# Revit family: Storage-Multi_Level_Workstations-Teknion-BSSCM_Cover_for_Height_Adjustable_Mechanism-R2018
name_source: partatom
category: Furniture
revit_build: Autodesk Revit 2018 (Build: 20170223_1515(x64)
units: mm (PartAtom-declared; Revit-internal decimal feet)

## family parameters
Always vertical = Yes
Cut with Voids When Loaded = No
OmniClass Number = 23.40.20.00
OmniClass Title = General Furniture and Specialties
Room Calculation Point = No
Shared = Yes
Work Plane-Based = No

## types (5) — shared parameters
Assembly Code = E2020200
Manufacturer = Teknion
Manufacturer Fax = 416.661.4586
Part Number = BSSCM
Product Documentation Link = https://www.teknion.com
Product Line = Expansion Casegoods
Product Page URL = https://www.teknion.com
Series = Expansion Casegoods
Sustainability Data = https://www.teknion.com
URL = www.teknion.com
Unit Weight URL = http://www.teknion.com
Warranty = http://www.teknion.com

## per-type parameters (varying)
| type | 1 3/16" Worksurface Thickness | Description | Full Secondary Desk Width Position | Insertion Point Offset | Model | Origin Point Offset |
| Center Position, No Width Reduction, in front of HA Mechanism | Yes | Cover for Height-Adjustable Mechanism, Center Position, No Width Reduction, In Front of Height-Adjustable Mechanism | No | 1.135 " | BSSCMCNY_____ | 1.97 " |
| End - Off-Module Position, End - 1 3/16" thick Secondary Desk, in front of HA Mechanism | Yes | Cover for Height-Adjustable Mechanism, End - Off-Module Position, End-1 3/16" thick Secondary Desk, In Front of Height-Adjustable Mechanism | No | 1.135 " | BSSCMEMY_____ | 7.315 " |
| End - Off-Module Position, End - 1 9/16" thick Secondary Desk, in front of HA Mechanism | No | Cover for Height-Adjustable Mechanism, End - Off-Module Position, End-1 9/16" thick Secondary Desk, In Front of Height-Adjustable Mechanism | No | 1.674 " | BSSCMEXY_____ | 7.315 " |
| Full Secondary Desk Width Position, End - 1 3/16" thick Secondary Desk, in front of HA Mechanism | Yes | Cover for Height-Adjustable Mechanism, Full Secondary Desk Width Position, End-1 3/16" thick Secondary Desk, In Front of Height-Adjustable Mechanism | Yes | 1.135 " | BSSCMFMY_____ | 7.315 " |
| Full Secondary Desk Width Position, End - 1 9/16" thick Secondary Desk, in front of HA Mechanism | No | Cover for Height-Adjustable Mechanism, Full Secondary Desk Width Position, End-1 9/16" thick Secondary Desk, In Front of Height-Adjustable Mechanism | Yes | 1.674 " | BSSCMFXY_____ | 7.315 " |

## geometry (parser evidence)
native form markers: Sweep x2
no freeform markers — native parametric forms only
